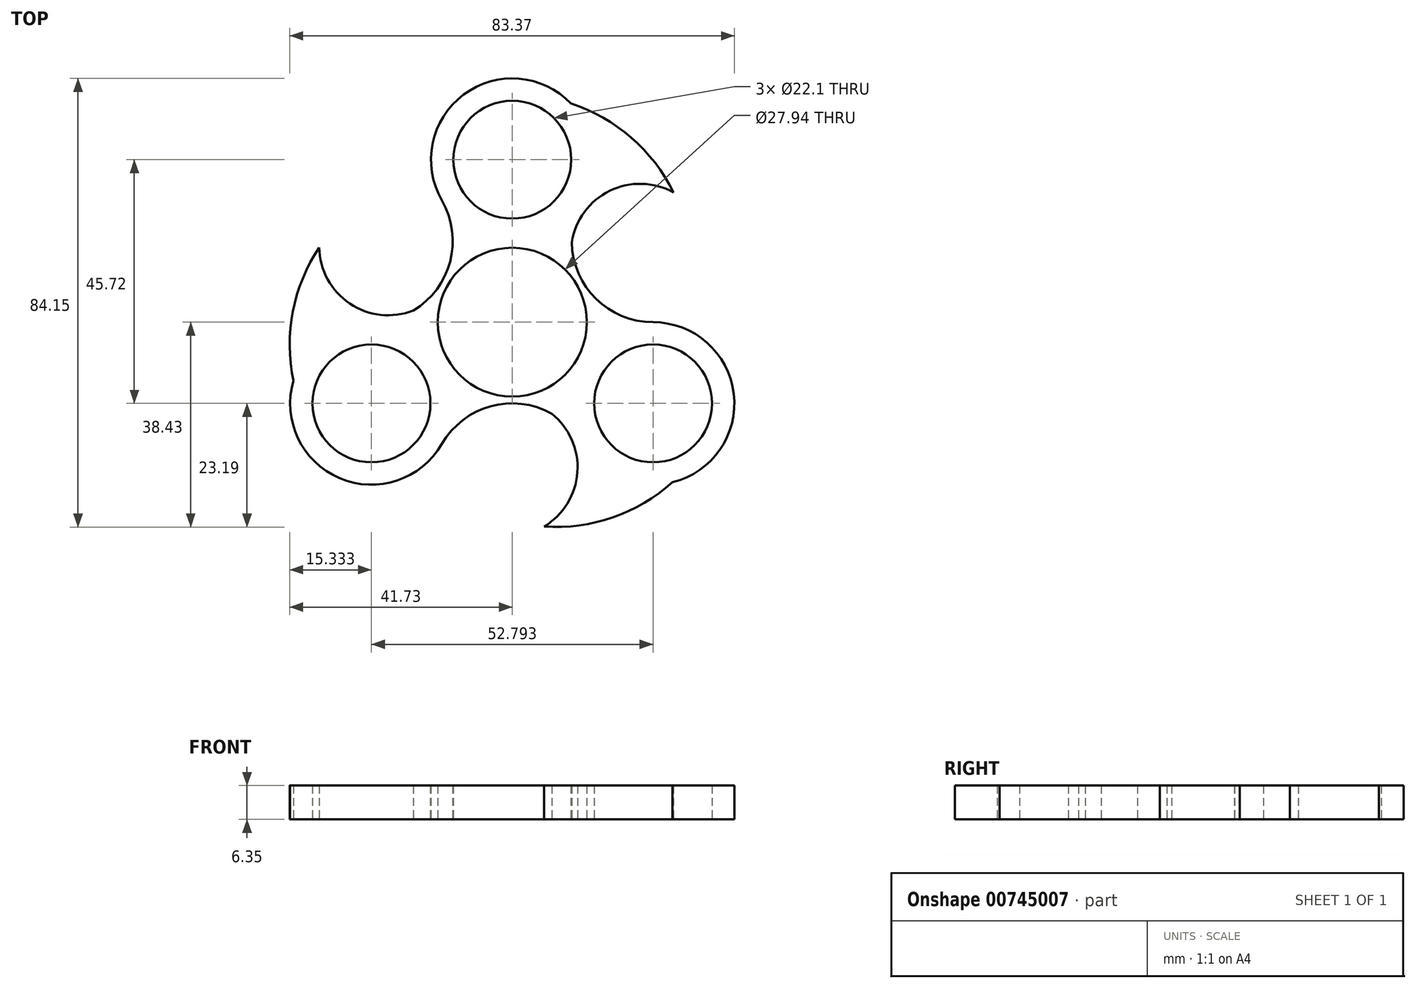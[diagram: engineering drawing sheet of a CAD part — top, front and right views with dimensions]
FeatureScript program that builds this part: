
annotation { "Feature Type Name" : "Feature", "Feature Type Description" : "" }
export const myFeature = defineFeature(function(context is Context, id is Id, definition is map)
    precondition{}
    {
        {
            var Q0;
            Q0=qCreatedBy(makeId("Top.planeOp"),FACE);
            var sketch = newSketch(context, id + "F0", { "sketchPlane" : qUnion([Q0])});
            skCircle(sketch, "E0", {"center": v(0, 0) * mm, "radius": 11.05 * mm});
            skCircle(sketch, "E1", {"center": v(0, 0) * mm, "radius": 13.97 * mm});
            skCircle(sketch, "E2", {"center": v(0, 30.48) * mm, "radius": 11.05 * mm});
            skArc(sketch, "E3", {"start": v(11, 41.03) * mm, "mid": v(-9.15, 42.67) * mm, "end": v(-13.2, 22.86) * mm});
            skCircle(sketch, "E4.1.0", {"center": v(-26.4, -15.24) * mm, "radius": 11.05 * mm});
            skArc(sketch, "E4.1.1", {"start": v(-41.03, -10.99) * mm, "mid": v(-32.38, -29.26) * mm, "end": v(-13.2, -22.86) * mm});
            skCircle(sketch, "E4.2.0", {"center": v(26.4, -15.24) * mm, "radius": 11.05 * mm});
            skArc(sketch, "E4.2.1", {"start": v(30.03, -30.04) * mm, "mid": v(41.53, -13.41) * mm, "end": v(26.4, 0) * mm});
            skArc(sketch, "E5", {"start": v(-18.55, 2.17) * mm, "mid": v(-11.64, 11.42) * mm, "end": v(-13.2, 22.86) * mm});
            skArc(sketch, "E6.1.0", {"start": v(7.4, -17.15) * mm, "mid": v(-4.07, -15.8) * mm, "end": v(-13.2, -22.86) * mm});
            skArc(sketch, "E6.2.0", {"start": v(11.16, 14.98) * mm, "mid": v(15.71, 4.37) * mm, "end": v(26.4, 0) * mm});
            skArc(sketch, "E7", {"start": v(30.24, 24.34) * mm, "mid": v(22.3, 34.62) * mm, "end": v(11, 41.03) * mm});
            skArc(sketch, "E8", {"start": v(30.24, 24.34) * mm, "mid": v(18.26, 24.64) * mm, "end": v(11.16, 14.98) * mm});
            skArc(sketch, "E9.1.0", {"start": v(-36.2, 14.01) * mm, "mid": v(-41.14, 2) * mm, "end": v(-41.03, -10.99) * mm});
            skArc(sketch, "E9.1.1", {"start": v(-36.2, 14.01) * mm, "mid": v(-30.46, 3.5) * mm, "end": v(-18.55, 2.17) * mm});
            skArc(sketch, "E9.2.0", {"start": v(5.96, -38.36) * mm, "mid": v(18.84, -36.62) * mm, "end": v(30.03, -30.04) * mm});
            skArc(sketch, "E9.2.1", {"start": v(5.96, -38.36) * mm, "mid": v(12.2, -28.13) * mm, "end": v(7.4, -17.15) * mm});
            skPoint(sketch, "E10.orphan", {"position": v(13.2, 22.86) * mm});
            skPoint(sketch, "E11.orphan", {"position": v(13.2, -22.86) * mm});
            skPoint(sketch, "E12.orphan", {"position": v(-26.4, 0) * mm});
            skSolve(sketch);
        }
        {
            var Q0;
            Q0=qSketchRegion(id+"F0",true);
            extrude(context, id + "F1", {"entities" : qUnion([Q0]), "depth" : 6.35 * mm, "offsetDistance" : 25.4 * mm});
        }
    });
